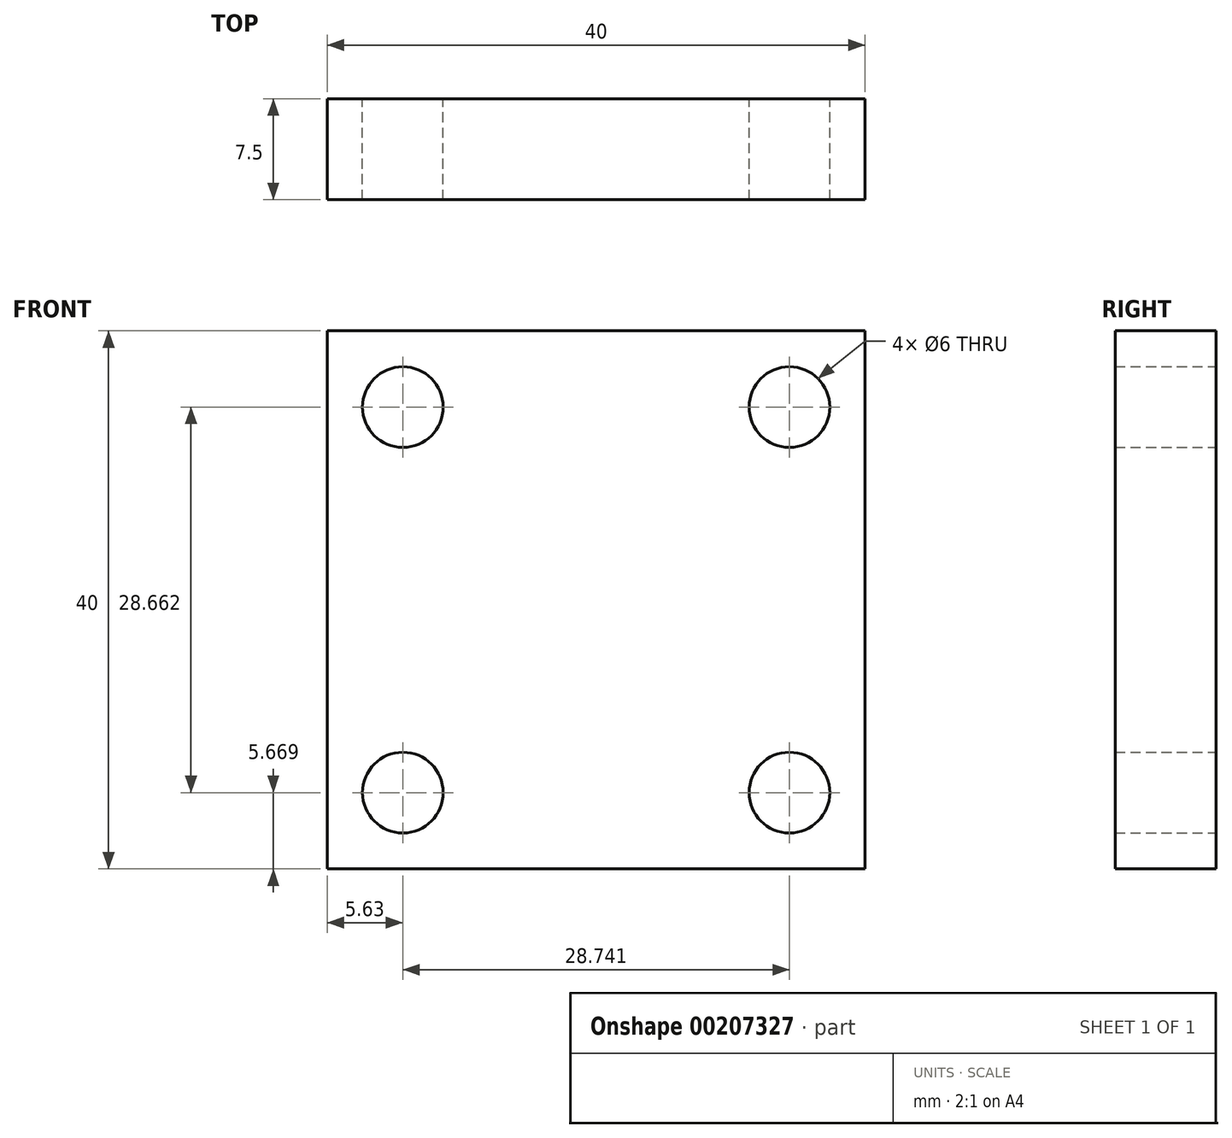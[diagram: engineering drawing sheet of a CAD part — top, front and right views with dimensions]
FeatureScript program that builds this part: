
annotation { "Feature Type Name" : "Feature", "Feature Type Description" : "" }
export const myFeature = defineFeature(function(context is Context, id is Id, definition is map)
    precondition{}
    {
        {
            var Q0;
            Q0=qCreatedBy(makeId("Front.planeOp"),FACE);
            var sketch = newSketch(context, id + "F0", { "sketchPlane" : qUnion([Q0])});
            skLineSegment(sketch, "E0.bottom", {"start": v(-20, 20) * mm, "end": v(20, 20) * mm});
            skLineSegment(sketch, "E0.top", {"start": v(-20, -20) * mm, "end": v(20, -20) * mm});
            skLineSegment(sketch, "E0.left", {"start": v(-20, 20) * mm, "end": v(-20, -20) * mm});
            skLineSegment(sketch, "E0.right", {"start": v(20, 20) * mm, "end": v(20, -20) * mm});
            skPoint(sketch, "E0.middle", {"position": v(0, 0) * mm});
            skCircle(sketch, "E1", {"center": v(-14.37, 14.33) * mm, "radius": 3 * mm});
            skCircle(sketch, "E2", {"center": v(14.37, 14.33) * mm, "radius": 3 * mm});
            skCircle(sketch, "E3", {"center": v(14.37, -14.33) * mm, "radius": 3 * mm});
            skCircle(sketch, "E4", {"center": v(-14.37, -14.33) * mm, "radius": 3 * mm});
            skSolve(sketch);
        }
        {
            var Q0;
            Q0=makeQuery(id+"F0.imprint","IMPRINT",FACE,{"disambiguationData":[TD([[makeQuery(id+"F0.imprint","IMPRINT",EDGE,{"derivedFrom":sQuery(id+"F0.wireOp",EDGE,"E0.bottom")}),-1.0]])]});
            extrude(context, id + "F1", {"entities" : qUnion([Q0]), "depth" : 7.5 * mm});
        }
    });
